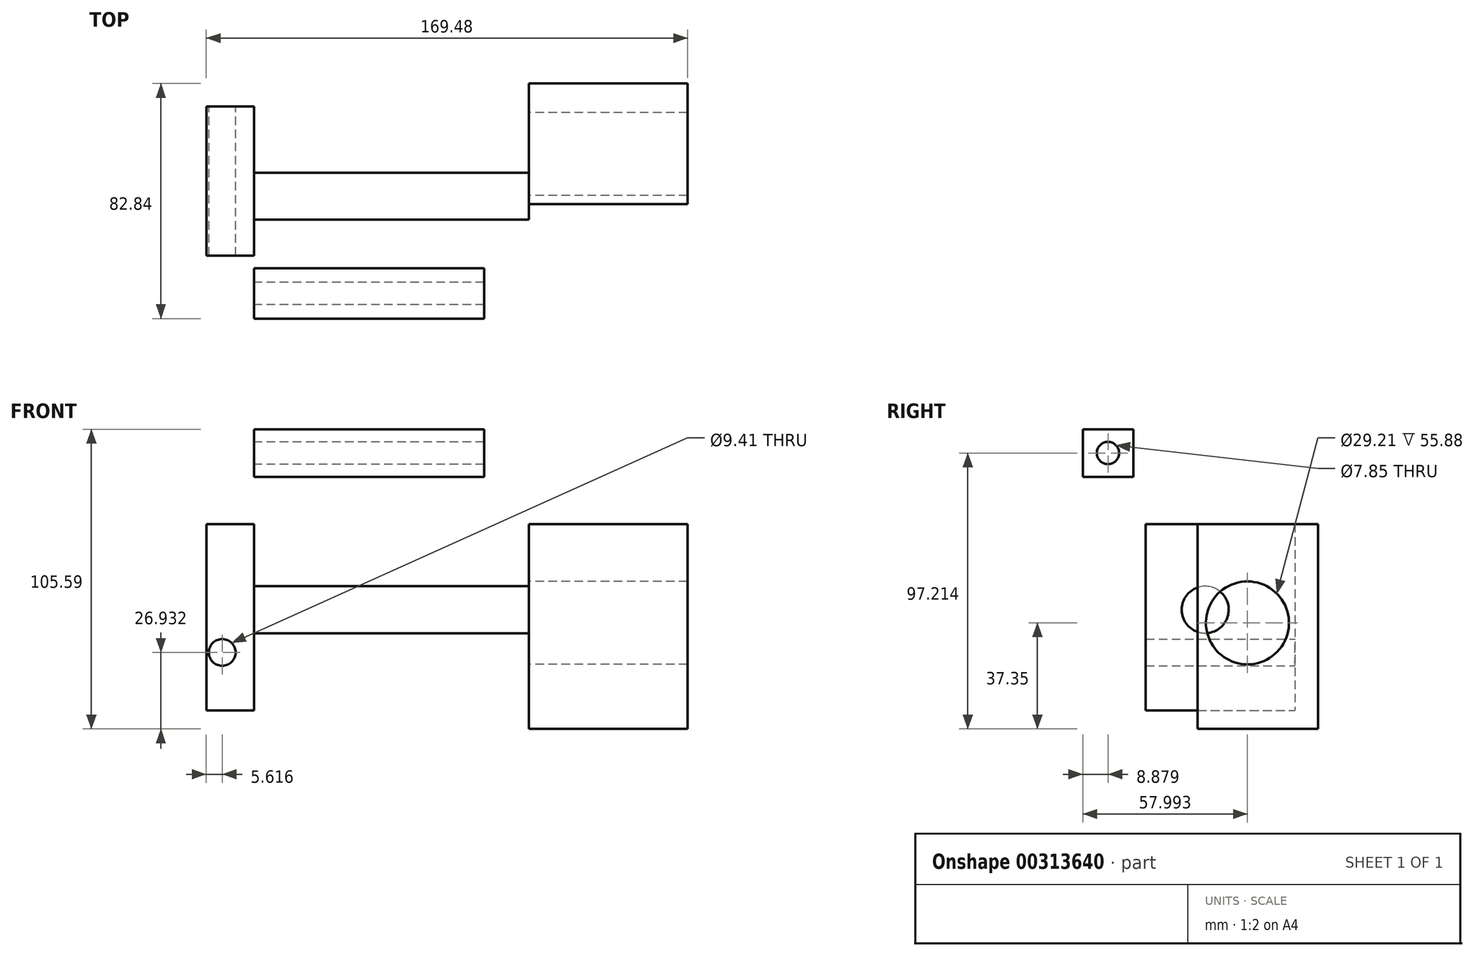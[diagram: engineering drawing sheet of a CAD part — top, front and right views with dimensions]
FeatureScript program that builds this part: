
annotation { "Feature Type Name" : "Feature", "Feature Type Description" : "" }
export const myFeature = defineFeature(function(context is Context, id is Id, definition is map)
    precondition{}
    {
        {
            var Q0;
            Q0=qCreatedBy(makeId("Right.planeOp"),FACE);
            var sketch = newSketch(context, id + "F0", { "sketchPlane" : qUnion([Q0])});
            skCircle(sketch, "E0", {"center": v(0, 9.53) * mm, "radius": 34.7 * mm});
            skCircle(sketch, "E1", {"center": v(0, 9.53) * mm, "radius": 60.04 * mm});
            skSolve(sketch);
        }
        {
            var Q0;
            Q0=qCreatedBy(makeId("Right.planeOp"),FACE);
            var sketch = newSketch(context, id + "F1", { "sketchPlane" : qUnion([Q0])});
            skLineSegment(sketch, "E2.bottom", {"start": v(-74.75, 16.66) * mm, "end": v(-57, 16.66) * mm});
            skLineSegment(sketch, "E2.top", {"start": v(-74.75, 33.4) * mm, "end": v(-57, 33.4) * mm});
            skLineSegment(sketch, "E2.left", {"start": v(-74.75, 16.66) * mm, "end": v(-74.75, 33.4) * mm});
            skLineSegment(sketch, "E2.right", {"start": v(-57, 16.66) * mm, "end": v(-57, 33.4) * mm});
            skPoint(sketch, "E2.middle", {"position": v(-65.87, 25.03) * mm});
            skCircle(sketch, "E3", {"center": v(-65.87, 25.03) * mm, "radius": 3.93 * mm});
            skSolve(sketch);
        }
        {
            var Q0;
            Q0=makeQuery(id+"F1.imprint","IMPRINT",FACE,{"disambiguationData":[TD([[makeQuery(id+"F1.imprint","IMPRINT",EDGE,{"derivedFrom":sQuery(id+"F1.wireOp",EDGE,"E2.bottom")}),1.0]])]});
            extrude(context, id + "F2", {"entities" : qUnion([Q0]), "depth" : 81.03 * mm});
        }
        {
            var Q0;
            Q0=qCreatedBy(makeId("Front.planeOp"),FACE);
            var sketch = newSketch(context, id + "F3", { "sketchPlane" : qUnion([Q0])});
            skLineSegment(sketch, "E4.bottom", {"start": v(0, 0) * mm, "end": v(-16.83, 0) * mm});
            skLineSegment(sketch, "E4.top", {"start": v(0, -65.67) * mm, "end": v(-16.83, -65.67) * mm});
            skLineSegment(sketch, "E4.left", {"start": v(0, 0) * mm, "end": v(0, -65.67) * mm});
            skLineSegment(sketch, "E4.right", {"start": v(-16.83, 0) * mm, "end": v(-16.83, -65.67) * mm});
            skCircle(sketch, "E5", {"center": v(-11.21, -45.25) * mm, "radius": 4.7 * mm});
            skSolve(sketch);
        }
        {
            var Q0;
            Q0=makeQuery(id+"F3.imprint","IMPRINT",FACE,{"disambiguationData":[TD([[makeQuery(id+"F3.imprint","IMPRINT",EDGE,{"derivedFrom":sQuery(id+"F3.wireOp",EDGE,"E4.bottom")}),1.0]])]});
            extrude(context, id + "F4", {"entities" : qUnion([Q0]), "depth" : 25.4 * mm});
        }
        {
            var Q0;
            Q0=makeQuery(id+"F4.opExtrude","CAP_FACE",FACE,{"disambiguationData":[OSD([sQuery(id+"F3.wireOp",EDGE,"E4.bottom"),sQuery(id+"F3.wireOp",EDGE,"E4.top"),sQuery(id+"F3.wireOp",EDGE,"E4.left"),sQuery(id+"F3.wireOp",EDGE,"E4.right"),sQuery(id+"F3.wireOp",EDGE,"E5")])],"isStart":false});
            var sketch = newSketch(context, id + "F5", { "sketchPlane" : qUnion([Q0])});
            skCircle(sketch, "E6", {"center": v(-11.88, -30.07) * mm, "radius": 3.4 * mm});
            skSolve(sketch);
        }
        {
            var Q0;
            Q0 = qSketchRegion(id + "F5", true);
            var Q1;
            Q1=makeQuery(id+"F5.imprint","IMPRINT",FACE,{"disambiguationData":[TD([[makeQuery(id+"F5.imprint","IMPRINT",EDGE,{"derivedFrom":sQuery(id+"F5.wireOp",EDGE,"E6")}),-1.0]])]});
            extrude(context, id + "F6", {"entities" : qUnion([Q0, Q1]), "operationType" : NewBodyOperationType.ADD, "depth" : 1.78 * mm});
        }
        {
            var Q0;
            Q0=makeQuery(id+"F6.opExtrude","CAP_FACE",FACE,{"disambiguationData":[OSD([sQuery(id+"F3.wireOp",EDGE,"E4.bottom"),sQuery(id+"F3.wireOp",EDGE,"E4.top"),sQuery(id+"F3.wireOp",EDGE,"E4.left"),sQuery(id+"F3.wireOp",EDGE,"E4.right"),sQuery(id+"F3.wireOp",EDGE,"E5")])],"isStart":false});
            var sketch = newSketch(context, id + "F7", { "sketchPlane" : qUnion([Q0])});
            skCircle(sketch, "E7", {"center": v(-11.61, -23.15) * mm, "radius": 4.17 * mm});
            skSolve(sketch);
        }
        {
            var Q0;
            Q0=sQuery(id+"F7.wireOp",EDGE,"E7");
            extrude(context, id + "F8", {"bodyType" : ToolBodyType.SURFACE, "surfaceEntities" : qUnion([Q0]), "oppositeDirection" : true, "depth" : 57.15 * mm});
        }
        {
            var Q0;
            Q0=makeQuery(id+"F6.opExtrude","CAP_FACE",FACE,{"disambiguationData":[OSD([sQuery(id+"F3.wireOp",EDGE,"E4.bottom"),sQuery(id+"F3.wireOp",EDGE,"E4.top"),sQuery(id+"F3.wireOp",EDGE,"E4.left"),sQuery(id+"F3.wireOp",EDGE,"E4.right"),sQuery(id+"F3.wireOp",EDGE,"E5")])],"isStart":false});
            extrude(context, id + "F9", {"entities" : qUnion([Q0]), "operationType" : NewBodyOperationType.ADD, "depth" : 25.4 * mm});
        }
        {
            var Q0;
            Q0=makeQuery(id+"F9.opExtrude","CAP_FACE",FACE,{"disambiguationData":[OSD([sQuery(id+"F3.wireOp",EDGE,"E4.bottom"),sQuery(id+"F3.wireOp",EDGE,"E4.top"),sQuery(id+"F3.wireOp",EDGE,"E4.left"),sQuery(id+"F3.wireOp",EDGE,"E4.right"),sQuery(id+"F3.wireOp",EDGE,"E5")])],"isStart":false});
            var sketch = newSketch(context, id + "F10", { "sketchPlane" : qUnion([Q0])});
            skCircle(sketch, "E8", {"center": v(-9.78, -22.24) * mm, "radius": 4.42 * mm});
            skSolve(sketch);
        }
        {
            var Q0;
            Q0=sQuery(id+"F10.wireOp",EDGE,"E8");
            extrude(context, id + "F11", {"bodyType" : ToolBodyType.SURFACE, "surfaceEntities" : qUnion([Q0]), "depth" : 25.4 * mm});
        }
        {
            var Q0;
            {var subQ0=sQuery(id+"F3.wireOp",EDGE,"E4.left");Q0=makeQuery(id+"F9.boolean.opBoolean","MERGE",FACE,{"derivedFrom":[makeQuery(id+"F6.boolean.opBoolean","MERGE",FACE,{"derivedFrom":[makeQuery(id+"F4.opExtrude","SWEPT_FACE",FACE,{"disambiguationData":[OSD([subQ0])]}),makeQuery(id+"F6.opExtrude","SWEPT_FACE",FACE,{"disambiguationData":[OSD([subQ0])]})]}),makeQuery(id+"F9.opExtrude","SWEPT_FACE",FACE,{"disambiguationData":[OSD([subQ0])]})]});}
            var sketch = newSketch(context, id + "F12", { "sketchPlane" : qUnion([Q0])});
            skCircle(sketch, "E9", {"center": v(-31.65, -30.18) * mm, "radius": 8.27 * mm});
            skSolve(sketch);
        }
        {
            var Q0;
            Q0 = qSketchRegion(id + "F12", true);
            extrude(context, id + "F13", {"entities" : qUnion([Q0]), "operationType" : NewBodyOperationType.ADD, "depth" : 96.77 * mm});
        }
        {
            var Q0;
            Q0=makeQuery(id+"F13.opExtrude","CAP_FACE",FACE,{"disambiguationData":[OSD([sQuery(id+"F12.wireOp",EDGE,"E9")])],"isStart":false});
            var sketch = newSketch(context, id + "F14", { "sketchPlane" : qUnion([Q0])});
            skLineSegment(sketch, "E10.bottom", {"start": v(-34.4, 0) * mm, "end": v(8.1, 0) * mm});
            skLineSegment(sketch, "E10.top", {"start": v(-34.4, -72.18) * mm, "end": v(8.1, -72.18) * mm});
            skLineSegment(sketch, "E10.left", {"start": v(-34.4, 0) * mm, "end": v(-34.4, -72.18) * mm});
            skLineSegment(sketch, "E10.right", {"start": v(8.1, 0) * mm, "end": v(8.1, -72.18) * mm});
            skCircle(sketch, "E11", {"center": v(-16.76, -34.83) * mm, "radius": 14.6 * mm});
            skSolve(sketch);
        }
        {
            var Q0;
            Q0 = qSketchRegion(id + "F14", true);
            extrude(context, id + "F15", {"entities" : qUnion([Q0]), "operationType" : NewBodyOperationType.ADD, "depth" : 55.88 * mm});
        }
    });
